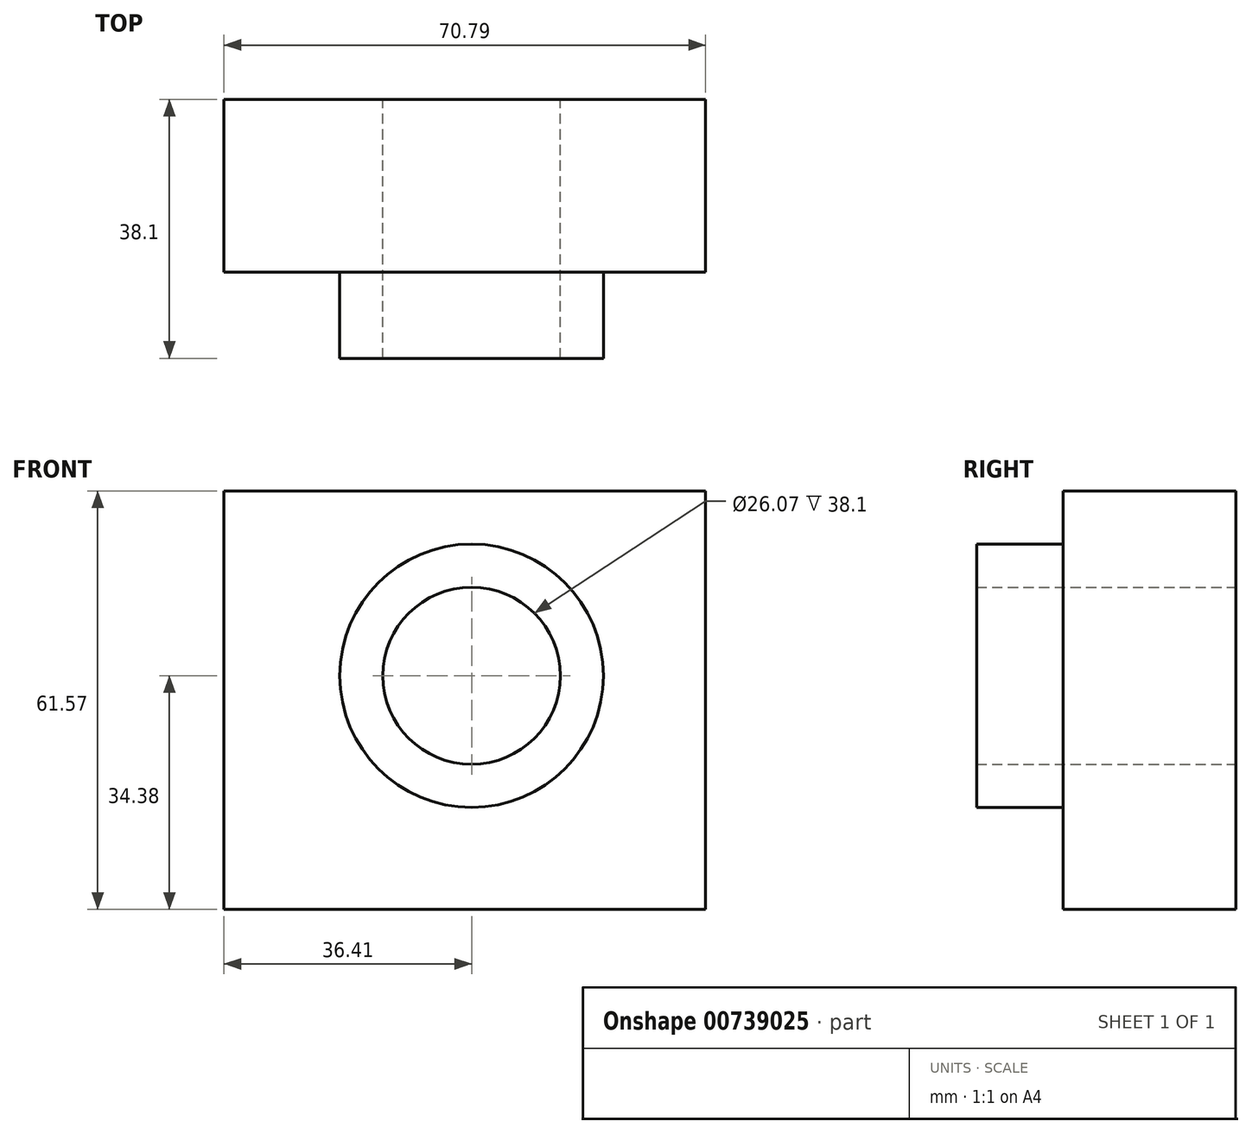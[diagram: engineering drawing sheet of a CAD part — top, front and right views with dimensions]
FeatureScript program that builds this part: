
annotation { "Feature Type Name" : "Feature", "Feature Type Description" : "" }
export const myFeature = defineFeature(function(context is Context, id is Id, definition is map)
    precondition{}
    {
        {
            var Q0;
            Q0=qCreatedBy(makeId("Front.planeOp"),FACE);
            var sketch = newSketch(context, id + "F0", { "sketchPlane" : qUnion([Q0])});
            skLineSegment(sketch, "E0.bottom", {"start": v(-36.41, 27.2) * mm, "end": v(34.38, 27.2) * mm});
            skLineSegment(sketch, "E0.top", {"start": v(-36.41, -34.38) * mm, "end": v(34.38, -34.38) * mm});
            skLineSegment(sketch, "E0.left", {"start": v(-36.41, 27.2) * mm, "end": v(-36.41, -34.38) * mm});
            skLineSegment(sketch, "E0.right", {"start": v(34.38, 27.2) * mm, "end": v(34.38, -34.38) * mm});
            skSolve(sketch);
        }
        {
            var Q0;
            Q0 = qSketchRegion(id + "F0", true);
            extrude(context, id + "F1", {"entities" : qUnion([Q0]), "depth" : 25.4 * mm, "offsetDistance" : 25.4 * mm});
        }
        {
            var Q0;
            Q0=qCreatedBy(makeId("Front.planeOp"),FACE);
            var sketch = newSketch(context, id + "F2", { "sketchPlane" : qUnion([Q0])});
            skCircle(sketch, "E1", {"center": v(0, 0) * mm, "radius": 19.37 * mm});
            skSolve(sketch);
        }
        {
            var Q0;
            Q0 = qSketchRegion(id + "F2", true);
            extrude(context, id + "F3", {"entities" : qUnion([Q0]), "operationType" : NewBodyOperationType.ADD, "depth" : 38.1 * mm, "offsetDistance" : 25.4 * mm});
        }
        {
            var Q0;
            Q0=qCreatedBy(makeId("Front.planeOp"),FACE);
            var sketch = newSketch(context, id + "F4", { "sketchPlane" : qUnion([Q0])});
            skCircle(sketch, "E2", {"center": v(0, 0) * mm, "radius": 13.03 * mm});
            skSolve(sketch);
        }
        {
            var Q0;
            Q0 = qSketchRegion(id + "F4", true);
            extrude(context, id + "F5", {"entities" : qUnion([Q0]), "operationType" : NewBodyOperationType.REMOVE, "depth" : 38.1 * mm, "offsetDistance" : 25.4 * mm});
        }
    });
